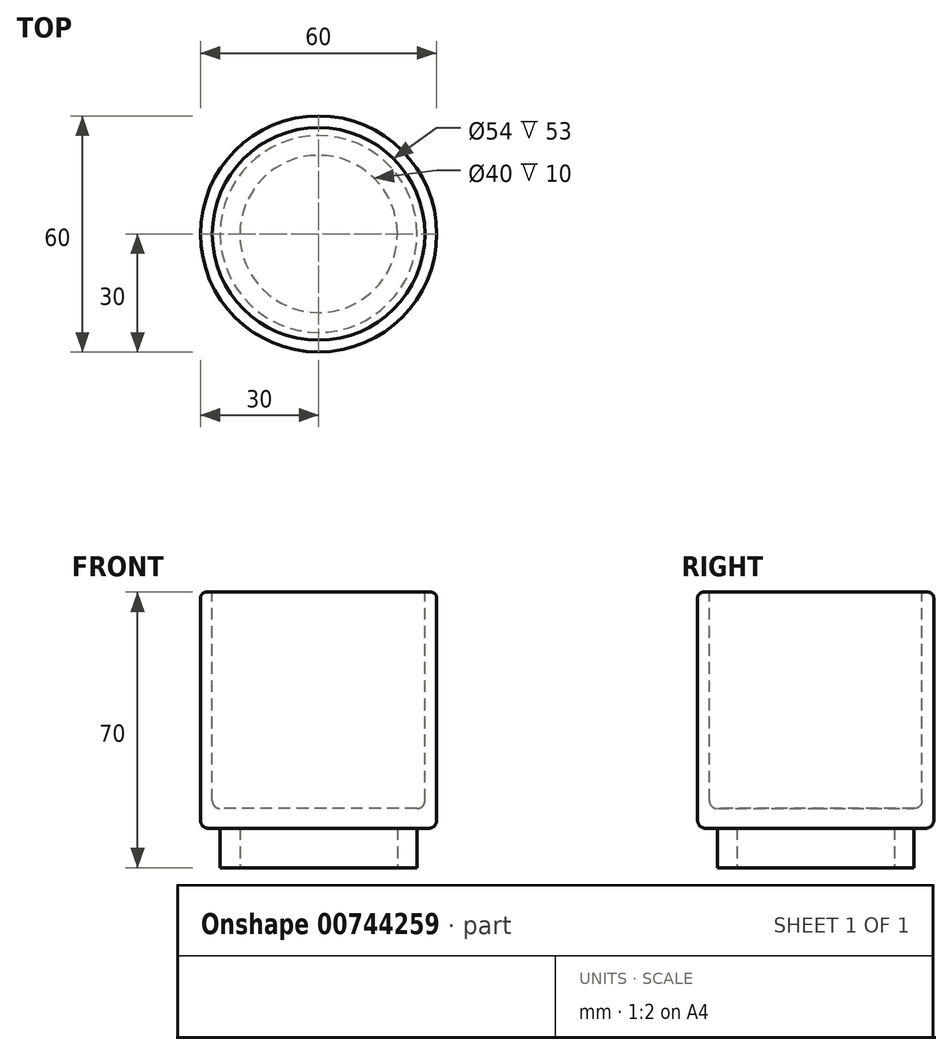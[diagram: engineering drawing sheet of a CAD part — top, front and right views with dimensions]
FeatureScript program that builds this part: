
annotation { "Feature Type Name" : "Feature", "Feature Type Description" : "" }
export const myFeature = defineFeature(function(context is Context, id is Id, definition is map)
    precondition{}
    {
        {
            var Q0;
            Q0=qCreatedBy(makeId("Top.planeOp"),FACE);
            var sketch = newSketch(context, id + "F0", { "sketchPlane" : qUnion([Q0])});
            skCircle(sketch, "E0", {"center": v(0, 0) * mm, "radius": 30 * mm});
            skSolve(sketch);
        }
        {
            var Q0;
            Q0 = qSketchRegion(id + "F0", true);
            extrude(context, id + "F1", {"entities" : qUnion([Q0]), "depth" : 60 * mm, "offsetDistance" : 25 * mm});
        }
        {
            var Q0;
            Q0=makeQuery(id+"F1.opExtrude","CAP_FACE",FACE,{"disambiguationData":[OSD([sQuery(id+"F0.wireOp",EDGE,"E0")])],"isStart":false});
            var sketch = newSketch(context, id + "F2", { "sketchPlane" : qUnion([Q0])});
            skCircle(sketch, "E1", {"center": v(0, 0) * mm, "radius": 27 * mm});
            skSolve(sketch);
        }
        {
            var Q0;
            Q0 = qSketchRegion(id + "F2", true);
            var Q1;
            Q1=makeQuery(id+"F1.opExtrude","CAP_FACE",FACE,{"disambiguationData":[OSD([sQuery(id+"F0.wireOp",EDGE,"E0")])],"isStart":true});
            extrude(context, id + "F3", {"entities" : qUnion([Q0, Q1]), "operationType" : NewBodyOperationType.REMOVE, "oppositeDirection" : true, "depth" : 55 * mm, "offsetDistance" : 25 * mm});
        }
        {
            var Q0;
            Q0=makeQuery(id+"F1.opExtrude","CAP_FACE",FACE,{"disambiguationData":[OSD([sQuery(id+"F0.wireOp",EDGE,"E0")])],"isStart":true});
            var sketch = newSketch(context, id + "F4", { "sketchPlane" : qUnion([Q0])});
            skCircle(sketch, "E2", {"center": v(0, 0) * mm, "radius": 25 * mm});
            skSolve(sketch);
        }
        {
            var Q0;
            Q0 = qSketchRegion(id + "F4", true);
            extrude(context, id + "F5", {"entities" : qUnion([Q0]), "operationType" : NewBodyOperationType.ADD, "depth" : 10 * mm, "offsetDistance" : 25 * mm});
        }
        {
            var Q0;
            Q0=makeQuery(id+"F5.opExtrude","CAP_FACE",FACE,{"disambiguationData":[OSD([sQuery(id+"F4.wireOp",EDGE,"E2")])],"isStart":false});
            var sketch = newSketch(context, id + "F6", { "sketchPlane" : qUnion([Q0])});
            skCircle(sketch, "E3", {"center": v(0, 0) * mm, "radius": 20 * mm});
            skSolve(sketch);
        }
        {
            var Q0;
            Q0 = qSketchRegion(id + "F6", true);
            extrude(context, id + "F7", {"entities" : qUnion([Q0]), "operationType" : NewBodyOperationType.REMOVE, "oppositeDirection" : true, "depth" : 10 * mm, "offsetDistance" : 25 * mm});
        }
        {
            var Q0;
            Q0=makeQuery(id+"F1.opExtrude","CAP_EDGE",EDGE,{"disambiguationData":[OSD([sQuery(id+"F0.wireOp",EDGE,"E0")])],"isStart":false});
            var Q1;
            Q1=makeQuery(id+"F3.boolean.opBoolean","COPY",EDGE,{"derivedFrom":makeQuery(id+"F3.opExtrude","CAP_EDGE",EDGE,{"disambiguationData":[OSD([sQuery(id+"F2.wireOp",EDGE,"E1")])],"isStart":true})});
            fillet(context, id + "F8", {"entities" : qUnion([Q0, Q1]), "radius" : 1.5 * mm, "tangentPropagation" : true, "allowEdgeOverflow" : false});
        }
        {
            var Q0;
            Q0=makeQuery(id+"F1.opExtrude","CAP_EDGE",EDGE,{"disambiguationData":[OSD([sQuery(id+"F0.wireOp",EDGE,"E0")])],"isStart":true});
            fillet(context, id + "F9", {"entities" : qUnion([Q0]), "radius" : 2 * mm, "tangentPropagation" : true, "allowEdgeOverflow" : false});
        }
        {
            var Q0;
            Q0=makeQuery(id+"F3.boolean.opBoolean","COPY",EDGE,{"derivedFrom":makeQuery(id+"F3.opExtrude","CAP_EDGE",EDGE,{"disambiguationData":[OSD([sQuery(id+"F2.wireOp",EDGE,"E1")])],"isStart":false})});
            fillet(context, id + "F10", {"entities" : qUnion([Q0]), "radius" : 2 * mm, "tangentPropagation" : true, "allowEdgeOverflow" : false});
        }
    });
